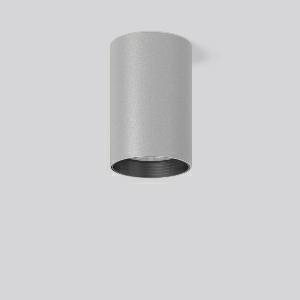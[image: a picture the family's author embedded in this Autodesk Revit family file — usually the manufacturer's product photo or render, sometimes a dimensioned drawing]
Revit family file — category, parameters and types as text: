
# Revit family: heledon_maxi_a_931221_004_3_2c1d
name_source: partatom
category: Lighting Fixtures
units: mm (PartAtom-declared; Revit-internal decimal feet)

## family parameters
Cut with Voids When Loaded = No
Host = Face
Light Source = No
Part Type = Normal
Room Calculation Point = No
Round Connector Dimension = Use Diameter
Shared = No

## types (1)
- HELEDON maxi A (1 x LED Modul 935, 2800 lm, 3500)
    Apparent Load = 25 VA
    Approval mark = CE
    CIE Flux Codes = 96 100 100 100 100
    Color Rendering = 92
    Color Temperature = 3500
    Default Elevation = 1800 mm
    Description = Series: HELEDON maxi
Cylindrical surface-mounted downlight. Housing: die-cast aluminium, powder-coated. Internal ceiling frame polycarbonate with bayonet mounting. Black plastic ring and recessed LED to prevent glare from the side. Optical assembly with lens made of plastic (polycarbonate) for the best homogeneous light distribution - can be changed without tools. Best colour rendering index Ra>90. Suitable for Ceiling mounting. Easy installation with a separate ceiling frame with bayonet mounting and plug connection. Driver integrated. Connected via plug-in connector. High quality converter without flickering and stroboscopic effect. The following accessories can be mounted without use of tools: interchangeable lenses, decorative glasses, honeycomb louvre, clear and frosted diffusers, white interchangeable plastic ring. 
Colour: silver
Diameter: 123 mm
Height: 183 mm
Lamp: LED
Socket: without socket
Colour temperature: 3500K
Colour rendering index (CRI): 92
System power: 25 W
Rated luminous flux: 2800 lm
Luminous efficiency: 112 lm/W
Control gear: Regulated power supply
Protection class: I
Type of protection: IP 20
    Height = 183 mm
    Lamp = 1 x LED Modul 935
    Lamp Light Flux = 2800 lm
    Lamp count = 1
    Length = 123 mm
    Lifetime = 50000 h
    Luminous efficacy = 112 lm/W
    Manufacturer = RZB
    ModVariant = No
    Model = 931221.004.3
    Mounting Place = Ceiling
    Mounting Type = Surface mounted
    Number of Poles = 1
    OnlyDefault = Yes
    Power Factor = 1
    Product Name = HELEDON maxi A
    Product group = Surface mounted downlights
    ProductGroupID = 302
    Protection Class = Protection class I
    Protection Degree = IP 20
    RLX_Detail_Level = 1
    RLX_Emergency_Light_Flux = 0 lm
    RLX_Emergency_Type = 0
    RLX_Emergency_Type_DB = No
    RlxData = <blob elided: 99217 chars, md5=e934e133>
    Socket = socket
    Standby Power = 0 W
    System Light Flux = 2800 lm
    System Power = 25 W
    Type Comments = Product without accessories
    Type Image = 931193.004.jpg
    URL = http://relux.com
    VarID = ---
    Voltage = 230 V
    Voltage Range = 220-240 V
    Weight = 0.00 kg
    Width = 0 mm  [stored 0 ft]

note: [stored X ft] marks values corroborated as IEEE doubles in the binary element streams (Revit-internal decimal feet)

## geometry (parser evidence)
native form markers: Blend x4, Sweep x10
no freeform markers — native parametric forms only
